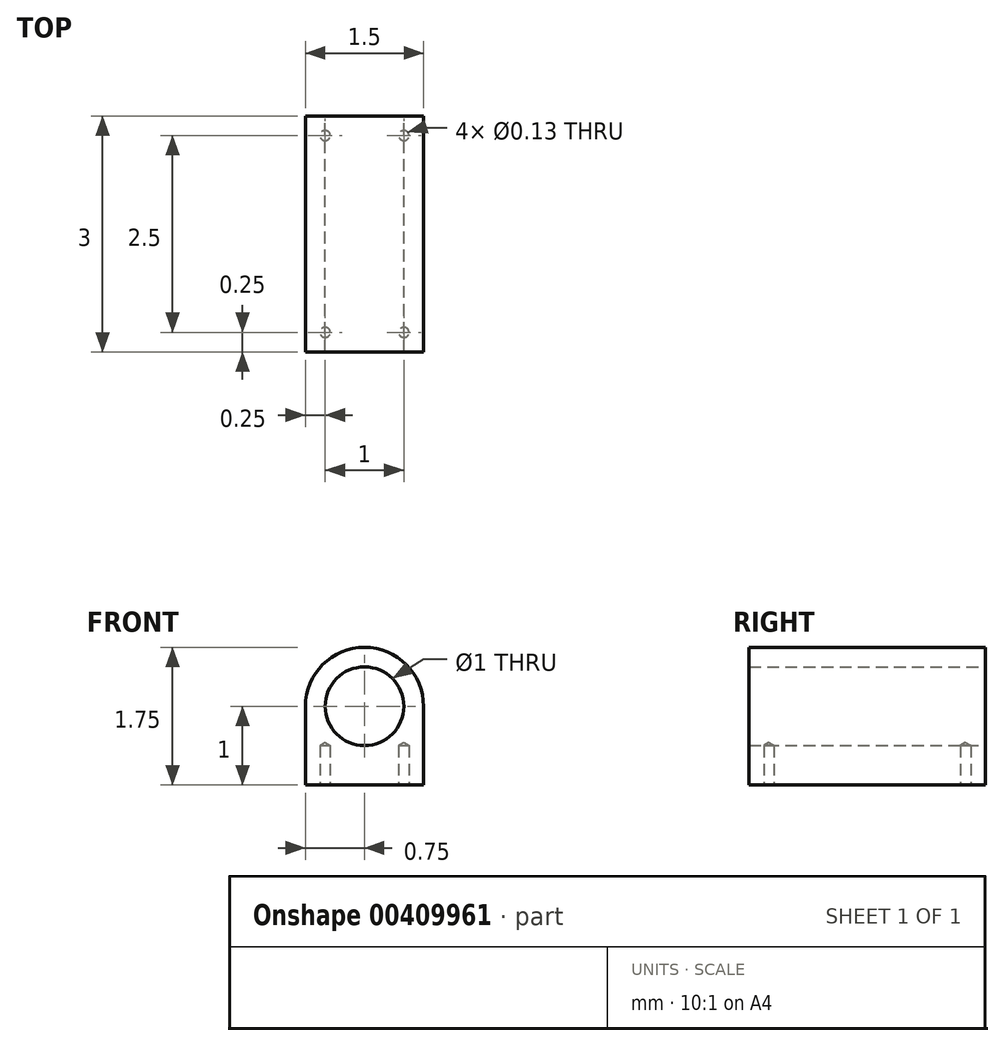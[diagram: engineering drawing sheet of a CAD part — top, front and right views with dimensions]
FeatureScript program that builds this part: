
annotation { "Feature Type Name" : "Feature", "Feature Type Description" : "" }
export const myFeature = defineFeature(function(context is Context, id is Id, definition is map)
    precondition{}
    {
        {
            var Q0;
            Q0=qCreatedBy(makeId("Front.planeOp"),FACE);
            var sketch = newSketch(context, id + "F0", { "sketchPlane" : qUnion([Q0])});
            skLineSegment(sketch, "E0.top", {"start": v(-0.75, 0) * mm, "end": v(0.75, 0) * mm});
            skLineSegment(sketch, "E0.left", {"start": v(-0.75, 1) * mm, "end": v(-0.75, 0) * mm});
            skLineSegment(sketch, "E0.right", {"start": v(0.75, 1) * mm, "end": v(0.75, 0) * mm});
            skArc(sketch, "E1", {"start": v(0.75, 1) * mm, "mid": v(0, 1.75) * mm, "end": v(-0.75, 1) * mm});
            skCircle(sketch, "E2", {"center": v(0, 1) * mm, "radius": 0.5 * mm});
            skSolve(sketch);
        }
        {
            var Q0;
            Q0 = qSketchRegion(id + "F0", true);
            extrude(context, id + "F1", {"entities" : qUnion([Q0]), "depth" : 3 * mm});
        }
        {
            var Q0;
            Q0=makeQuery(id+"F1.opExtrude","SWEPT_FACE",FACE,{"disambiguationData":[OSD([sQuery(id+"F0.wireOp",EDGE,"E0.top")])]});
            var sketch = newSketch(context, id + "F2", { "sketchPlane" : qUnion([Q0])});
            skPoint(sketch, "E3", {"position": v(-0.5, 2.75) * mm});
            skPoint(sketch, "E4", {"position": v(0.5, 2.75) * mm});
            skPoint(sketch, "E5", {"position": v(0.5, 0.25) * mm});
            skPoint(sketch, "E6", {"position": v(-0.5, 0.25) * mm});
            skSolve(sketch);
        }
        {
            var Q0;
            Q0=sQuery(id+"F2.wireOp",VERTEX,"E3");
            var Q1;
            Q1=sQuery(id+"F2.wireOp",VERTEX,"E4");
            var Q2;
            Q2=sQuery(id+"F2.wireOp",VERTEX,"E6");
            var Q3;
            Q3=sQuery(id+"F2.wireOp",VERTEX,"E5");
            var Q4;
            Q4=makeQuery(id+"F1.opExtrude","SWEPT_BODY",BODY,{"disambiguationData":[OSD([sQuery(id+"F0.wireOp",EDGE,"E0.top"),sQuery(id+"F0.wireOp",EDGE,"E0.left"),sQuery(id+"F0.wireOp",EDGE,"E0.right"),sQuery(id+"F0.wireOp",EDGE,"E1"),sQuery(id+"F0.wireOp",EDGE,"E2")])]});
            hole(context, id + "F3", {"style" : HoleStyle.SIMPLE, "endStyle" : HoleEndStyle.BLIND, "holeDiameter" : 0.13 * mm, "holeDepth" : 0.5 * mm, "isTappedThrough" : true, "tappedDepth" : 12 * mm, "tapClearance" : 3, "locations" : qUnion([Q0, Q1, Q2, Q3]), "scope" : qUnion([Q4])});
        }
    });
